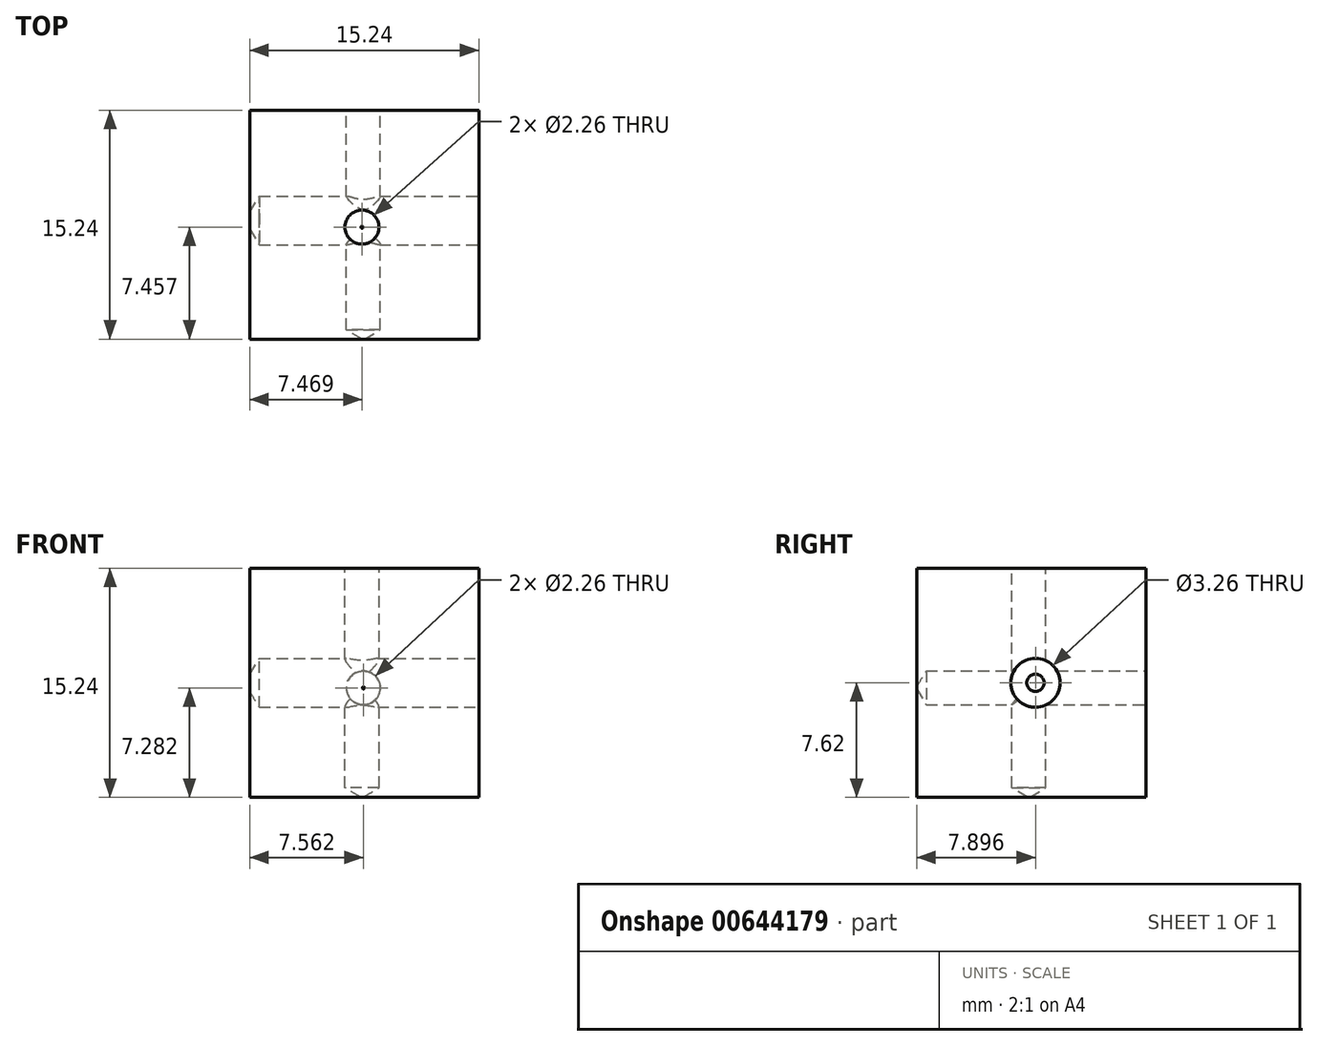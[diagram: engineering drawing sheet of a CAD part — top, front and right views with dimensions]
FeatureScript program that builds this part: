
annotation { "Feature Type Name" : "Feature", "Feature Type Description" : "" }
export const myFeature = defineFeature(function(context is Context, id is Id, definition is map)
    precondition{}
    {
        {
            var Q0;
            Q0=qCreatedBy(makeId("Right.planeOp"),FACE);
            var sketch = newSketch(context, id + "F0", { "sketchPlane" : qUnion([Q0])});
            skLineSegment(sketch, "E0.bottom", {"start": v(-16.7, 15.24) * mm, "end": v(-1.46, 15.24) * mm});
            skLineSegment(sketch, "E0.top", {"start": v(-16.7, 0) * mm, "end": v(-1.46, 0) * mm});
            skLineSegment(sketch, "E0.left", {"start": v(-16.7, 15.24) * mm, "end": v(-16.7, 0) * mm});
            skLineSegment(sketch, "E0.right", {"start": v(-1.46, 15.24) * mm, "end": v(-1.46, 0) * mm});
            skSolve(sketch);
        }
        {
            var Q0;
            Q0 = qSketchRegion(id + "F0", true);
            extrude(context, id + "F1", {"entities" : qUnion([Q0]), "depth" : 15.24 * mm, "offsetDistance" : 25.4 * mm});
        }
        {
            var Q0;
            Q0=makeQuery(id+"F1.opExtrude","CAP_FACE",FACE,{"disambiguationData":[OSD([sQuery(id+"F0.wireOp",EDGE,"E0.bottom"),sQuery(id+"F0.wireOp",EDGE,"E0.top"),sQuery(id+"F0.wireOp",EDGE,"E0.left"),sQuery(id+"F0.wireOp",EDGE,"E0.right")])],"isStart":false});
            var sketch = newSketch(context, id + "F2", { "sketchPlane" : qUnion([Q0])});
            skPoint(sketch, "E1", {"position": v(-8.8, 7.62) * mm});
            skPoint(sketch, "E1.positionSnap0", {"position": v(-1.46, 7.62) * mm});
            skSolve(sketch);
        }
        {
            var Q0;
            Q0=sQuery(id+"F2.wireOp",VERTEX,"E1");
            var Q1;
            Q1=makeQuery(id+"F1.opExtrude","SWEPT_BODY",BODY,{"disambiguationData":[OSD([sQuery(id+"F0.wireOp",EDGE,"E0.bottom"),sQuery(id+"F0.wireOp",EDGE,"E0.top"),sQuery(id+"F0.wireOp",EDGE,"E0.left"),sQuery(id+"F0.wireOp",EDGE,"E0.right")])]});
            hole(context, id + "F3", {"style" : HoleStyle.SIMPLE, "endStyle" : HoleEndStyle.BLIND, "standardTappedOrClearance" : lookupTablePath({ "standard" : "ANSI", "fit" : "Normal (ASME)", "size" : "#4", "type" : "Clearance" }), "standardBlindInLast" : lookupTablePath({ "fit" : "Free", "standard" : "ANSI", "size" : "#4", "type" : "Clearance" }), "holeDiameter" : 3.26 * mm, "majorDiameter" : 2.84 * mm, "holeDepth" : 14.6 * mm, "isTappedThrough" : true, "tappedDepth" : 12.7 * mm, "tapClearance" : 3, "locations" : qUnion([Q0]), "scope" : qUnion([Q1])});
        }
        {
            var Q0;
            Q0=qCreatedBy(makeId("Front.planeOp"),FACE);
            var sketch = newSketch(context, id + "F4", { "sketchPlane" : qUnion([Q0])});
            skPoint(sketch, "E2", {"position": v(7.56, 7.28) * mm});
            skSolve(sketch);
        }
        {
            var Q0;
            Q0=sQuery(id+"F4.wireOp",VERTEX,"E2");
            var Q1;
            Q1=makeQuery(id+"F1.opExtrude","SWEPT_BODY",BODY,{"disambiguationData":[OSD([sQuery(id+"F0.wireOp",EDGE,"E0.bottom"),sQuery(id+"F0.wireOp",EDGE,"E0.top"),sQuery(id+"F0.wireOp",EDGE,"E0.left"),sQuery(id+"F0.wireOp",EDGE,"E0.right")])]});
            hole(context, id + "F5", {"style" : HoleStyle.SIMPLE, "endStyle" : HoleEndStyle.BLIND, "oppositeDirection" : true, "standardTappedOrClearance" : lookupTablePath({ "standard" : "ANSI", "engagement" : "75%", "pitch" : "40 tpi", "size" : "#4", "type" : "Tapped" }), "standardBlindInLast" : lookupTablePath({ "standard" : "ANSI", "engagement" : "75%", "pitch" : "40 tpi", "size" : "#4", "type" : "Tapped" }), "holeDiameter" : 2.26 * mm, "majorDiameter" : 2.84 * mm, "showTappedDepth" : true, "holeDepth" : 14.6 * mm, "isTappedThrough" : true, "tappedDepth" : 12.7 * mm, "tapClearance" : 3, "locations" : qUnion([Q0]), "scope" : qUnion([Q1])});
        }
        {
            var Q0;
            Q0=makeQuery(id+"F1.opExtrude","SWEPT_FACE",FACE,{"disambiguationData":[OSD([sQuery(id+"F0.wireOp",EDGE,"E0.bottom")])]});
            var sketch = newSketch(context, id + "F6", { "sketchPlane" : qUnion([Q0])});
            skPoint(sketch, "E3", {"position": v(7.47, -9.24) * mm});
            skSolve(sketch);
        }
        {
            var Q0;
            Q0=sQuery(id+"F6.wireOp",VERTEX,"E3");
            var Q1;
            Q1=makeQuery(id+"F1.opExtrude","SWEPT_BODY",BODY,{"disambiguationData":[OSD([sQuery(id+"F0.wireOp",EDGE,"E0.bottom"),sQuery(id+"F0.wireOp",EDGE,"E0.top"),sQuery(id+"F0.wireOp",EDGE,"E0.left"),sQuery(id+"F0.wireOp",EDGE,"E0.right")])]});
            hole(context, id + "F7", {"style" : HoleStyle.SIMPLE, "endStyle" : HoleEndStyle.BLIND, "standardTappedOrClearance" : lookupTablePath({ "standard" : "ANSI", "engagement" : "75%", "pitch" : "40 tpi", "size" : "#4", "type" : "Tapped" }), "standardBlindInLast" : lookupTablePath({ "standard" : "ANSI", "engagement" : "75%", "pitch" : "40 tpi", "size" : "#4", "type" : "Tapped" }), "holeDiameter" : 2.26 * mm, "majorDiameter" : 2.84 * mm, "showTappedDepth" : true, "holeDepth" : 14.6 * mm, "isTappedThrough" : true, "tappedDepth" : 12.7 * mm, "tapClearance" : 3, "locations" : qUnion([Q0]), "scope" : qUnion([Q1])});
        }
    });
